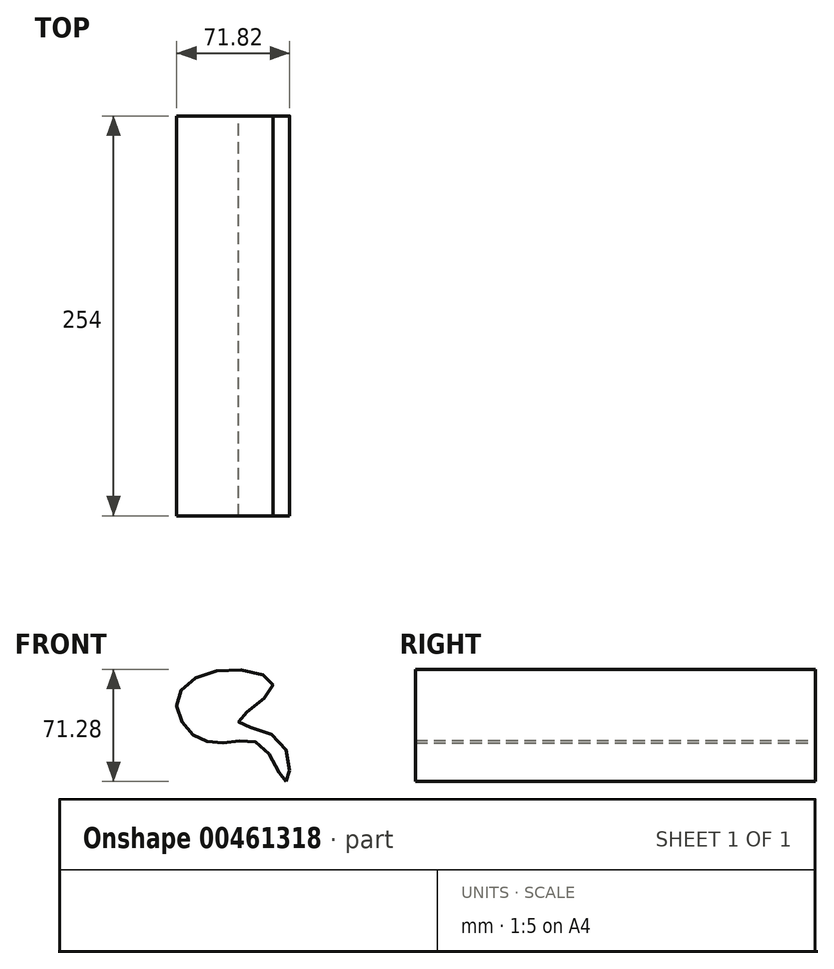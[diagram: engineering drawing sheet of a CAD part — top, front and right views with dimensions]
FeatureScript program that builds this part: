
annotation { "Feature Type Name" : "Feature", "Feature Type Description" : "" }
export const myFeature = defineFeature(function(context is Context, id is Id, definition is map)
    precondition{}
    {
        {
            var Q0;
            Q0=qCreatedBy(makeId("Front.planeOp"),FACE);
            var sketch = newSketch(context, id + "F0", { "sketchPlane" : qUnion([Q0])});
            skFitSpline(sketch, "E0", {"points": [v(0, 0) * mm, v(-14.86, 22.44) * mm, v(-39.17, 24.52) * mm, v(-60.98, 31.37) * mm, v(-68.46, 54.65) * mm, v(-34.18, 71.27) * mm, v(-8.41, 59.63) * mm, v(-30.02, 38.23) * mm, v(-3.22, 25.56) * mm, v(0, 0) * mm]});
            skSolve(sketch);
        }
        {
            var Q0;
            Q0=makeQuery(id+"F0.imprint","IMPRINT",FACE,{"disambiguationData":[TD([[makeQuery(id+"F0.imprint","IMPRINT",EDGE,{"derivedFrom":sQuery(id+"F0.wireOp",EDGE,"E0")}),-1.0]])]});
            extrude(context, id + "F1", {"entities" : qUnion([Q0]), "depth" : 254 * mm, "offsetDistance" : 25.4 * mm});
        }
    });
